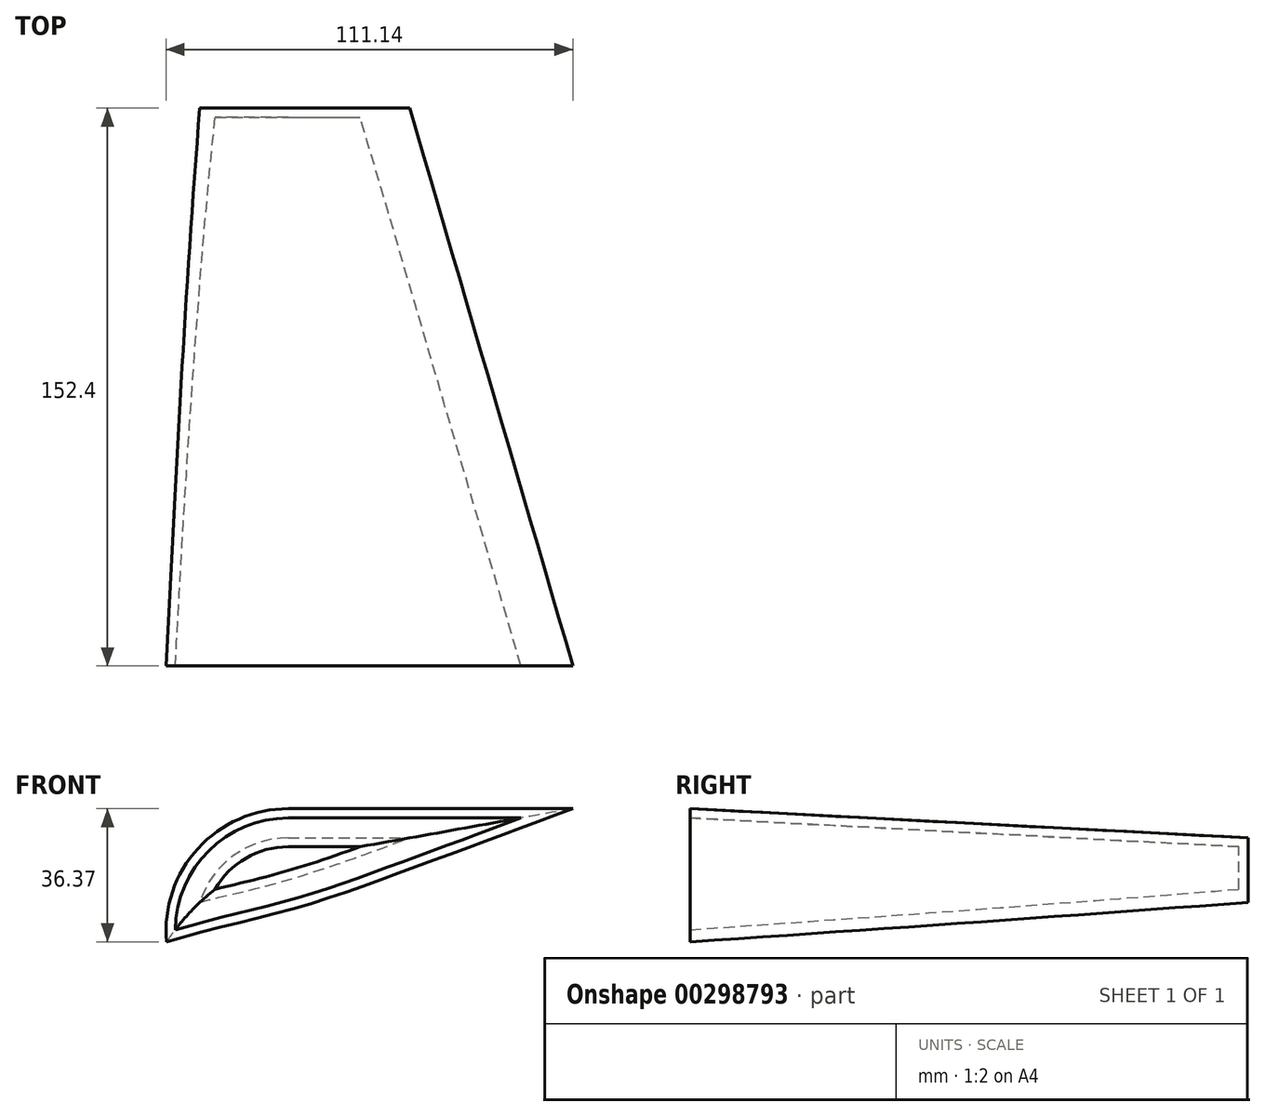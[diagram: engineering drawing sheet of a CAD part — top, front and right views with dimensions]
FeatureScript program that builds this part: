
annotation { "Feature Type Name" : "Feature", "Feature Type Description" : "" }
export const myFeature = defineFeature(function(context is Context, id is Id, definition is map)
    precondition{}
    {
        {
            var Q0;
            Q0=qCreatedBy(makeId("Front.planeOp"),FACE);
            var sketch = newSketch(context, id + "F0", { "sketchPlane" : qUnion([Q0])});
            skLineSegment(sketch, "E0.bottom", {"start": v(-17.6, 50.8) * mm, "end": v(-50.8, 50.8) * mm});
            skLineSegment(sketch, "E0.top", {"start": v(50.8, -50.8) * mm, "end": v(9.08, -50.8) * mm});
            skLineSegment(sketch, "E0.left", {"start": v(76.2, 25.4) * mm, "end": v(76.2, 4.68) * mm});
            skLineSegment(sketch, "E0.right", {"start": v(-76.2, -1.08) * mm, "end": v(-76.2, -25.4) * mm});
            skPoint(sketch, "E0.middle", {"position": v(0, 0) * mm});
            skPoint(sketch, "E1.visualSharp", {"position": v(-76.2, 50.8) * mm});
            skArc(sketch, "E1.filletArc", {"start": v(-50.8, 50.8) * mm, "mid": v(-65.75, 45.93) * mm, "end": v(-74.97, 33.2) * mm});
            skPoint(sketch, "E2.visualSharp", {"position": v(76.2, 50.8) * mm});
            skArc(sketch, "E2.filletArc", {"start": v(76.2, 25.4) * mm, "mid": v(71.37, 40.3) * mm, "end": v(58.72, 49.53) * mm});
            skPoint(sketch, "E3.visualSharp", {"position": v(-76.2, -50.8) * mm});
            skArc(sketch, "E3.filletArc", {"start": v(-76.2, -25.4) * mm, "mid": v(-71.06, -40.72) * mm, "end": v(-57.73, -49.84) * mm});
            skPoint(sketch, "E4.visualSharp", {"position": v(76.2, -50.8) * mm});
            skArc(sketch, "E4.filletArc", {"start": v(50.8, -50.8) * mm, "mid": v(65.44, -46.16) * mm, "end": v(74.72, -33.93) * mm});
            skFitSpline(sketch, "E5", {"points": [v(-88.5, 24) * mm, v(-49.93, 39.6) * mm, v(47.4, 65.09) * mm, v(66.92, 22.38) * mm, v(91.26, -25.83) * mm, v(50.8, -38.46) * mm, v(-50.4, -61.41) * mm, v(-63.02, -25.37) * mm, v(-88.5, 24) * mm]});
            skPoint(sketch, "E6.orphan", {"position": v(50.8, 50.8) * mm});
            skSolve(sketch);
        }
        {
            var Q0;
            Q0=makeQuery(id+"F0.imprint","IMPRINT",FACE,{"disambiguationData":[TD([[makeQuery(id+"F0.imprint","IMPRINT",EDGE,{"derivedFrom":sQuery(id+"F0.wireOp",EDGE,"E0.bottom")}),1.0]])]});
            extrude(context, id + "F1", {"entities" : qUnion([Q0]), "depth" : 152.4 * mm, "hasDraft" : true, "draftAngle" : 3 * degree});
        }
        {
            var Q0;
            Q0=makeQuery(id+"F1.opExtrude","CAP_FACE",FACE,{"disambiguationData":[OSD([sQuery(id+"F0.wireOp",EDGE,"E0.bottom"),sQuery(id+"F0.wireOp",EDGE,"E0.top"),sQuery(id+"F0.wireOp",EDGE,"E0.left"),sQuery(id+"F0.wireOp",EDGE,"E0.right"),sQuery(id+"F0.wireOp",EDGE,"E1.filletArc"),sQuery(id+"F0.wireOp",EDGE,"E2.filletArc"),sQuery(id+"F0.wireOp",EDGE,"E3.filletArc"),sQuery(id+"F0.wireOp",EDGE,"E4.filletArc"),sQuery(id+"F0.wireOp",EDGE,"E5"),sQuery(id+"F0.wireOp",EDGE,"E5"),sQuery(id+"F0.wireOp",EDGE,"E5"),sQuery(id+"F0.wireOp",EDGE,"E5")])],"isStart":false});
            shell(context, id + "F2", {"entities" : qUnion([Q0]), "thickness" : 2.54 * mm});
        }
    });
